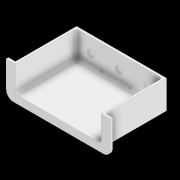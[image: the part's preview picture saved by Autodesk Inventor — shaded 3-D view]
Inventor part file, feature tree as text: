
AUTODESK INVENTOR PART (.ipt)
format: ipt  version: 2020 (Build 240168000, 168)  size: 455,680 bytes
history: native  units: mm
features: other x20, sketch x11, plane x7, fillet x5, extrude x5, sweep x2, mirror x2, pattern_linear x2, hole x1, projected_geometry x1
ambient origin geometry x8: Origin, YZ Plane, XZ Plane, XY Plane, X Axis, Y Axis, Z Axis, Center Point
bodies: Body1 (feature_tree), Body2 (feature_tree)
feature tree (56):
  other  "自動販賣機.ipt"
  fillet  "圓角1"  Radius=10.0mm
  fillet  "圓角2"  Radius=25.0mm
  extrude  "擠出2"  Depth=50.0mm
  fillet  "圓角3"  Radius=92.5mm
  fillet  "圓角4"  Radius=46.25mm
  hole  "孔1"  [1 undecoded]
  plane  "工作平面1"
  extrude  "擠出3"  Depth=50.0mm
  plane  "工作平面3"
  sketch  "草圖5"
  plane  "工作平面4"
  sweep  "掃掠1"
  plane  "工作平面10"
  mirror  "鏡射5"
  extrude  "擠出6"  Depth=85.0mm
  pattern_linear  "矩形陣列1"  Spacing1=5.0mm  [1 undecoded]
  mirror  "鏡射6"
  pattern_linear  "矩形陣列2"  Count1=20  [1 undecoded]
  sketch  "草圖11"
  extrude  "擠出4"  Depth=200.0mm
  fillet  "圓角5"  Radius=20.0mm
  plane  "工作平面8"
  plane  "工作平面9"
  sweep  "掃掠2"
  extrude  "擠出5"  Depth=27.5mm
  other  "實體22::自動販賣機.ipt"
  other  "標籤特徵1"
  sketch  "草圖1"
  sketch  "草圖3"
  sketch  "草圖4"
  projected_geometry  "投影迴路2"
  plane  "工作平面2"
  sketch  "草圖6"
  other  "實體2"
  sketch  "草圖7"
  sketch  "草圖8"
  sketch  "草圖9"
  sketch  "草圖10"
  sketch  "草圖12"
  other  "實體1"
  other  "投影切割邊1"
  other  "投影切割邊3"
  other  "投影切割邊4"
  other  "投影切割邊5"
  other  "投影切割邊6"
  other  "投影切割邊7"
  other  "投影切割邊8"
  other  "投影切割邊9"
  other  "投影切割邊10"
  other  "投影切割邊11"
  other  "投影切割邊12"
  other  "投影切割邊13"
  other  "投影切割邊14"
  other  "投影切割邊15"
  other  "投影切割邊16"
note: 3 required parameter values undecoded (feature->parameter linkage not recoverable at this tier; creation-order binding heuristic only, values carry confidence <= 0.55)
